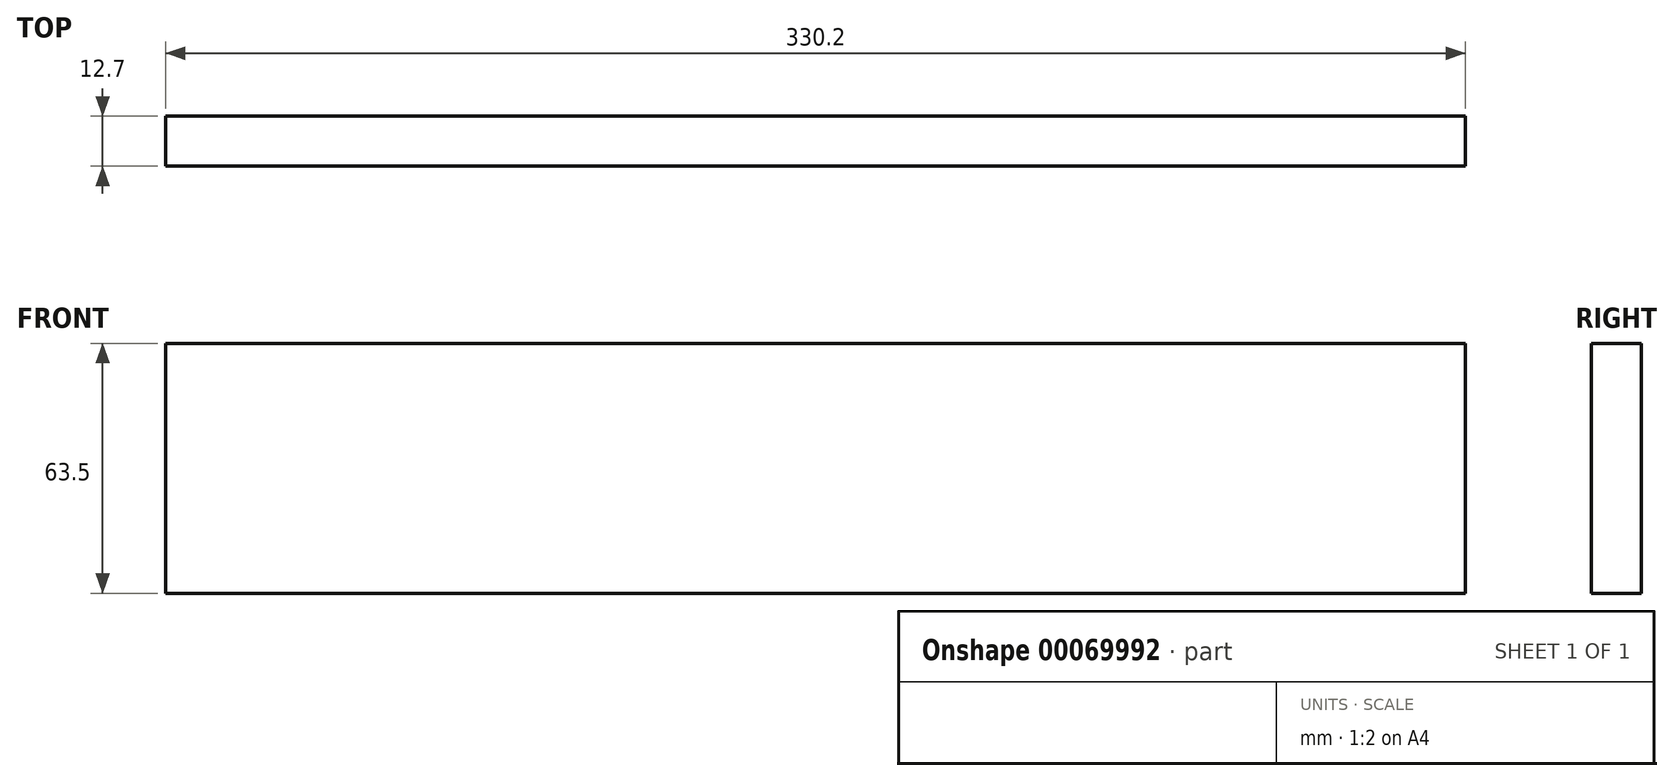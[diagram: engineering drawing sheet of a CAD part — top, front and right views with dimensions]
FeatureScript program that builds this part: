
annotation { "Feature Type Name" : "Feature", "Feature Type Description" : "" }
export const myFeature = defineFeature(function(context is Context, id is Id, definition is map)
    precondition{}
    {
        {
            var Q0;
            Q0=qCreatedBy(makeId("Front.planeOp"),FACE);
            var sketch = newSketch(context, id + "F0", { "sketchPlane" : qUnion([Q0])});
            skLineSegment(sketch, "E0.rect.bottom", {"start": v(165.1, 31.75) * mm, "end": v(-165.1, 31.75) * mm});
            skLineSegment(sketch, "E0.rect.top", {"start": v(165.1, -31.75) * mm, "end": v(-165.1, -31.75) * mm});
            skLineSegment(sketch, "E0.rect.left", {"start": v(165.1, 31.75) * mm, "end": v(165.1, -31.75) * mm});
            skLineSegment(sketch, "E0.rect.right", {"start": v(-165.1, 31.75) * mm, "end": v(-165.1, -31.75) * mm});
            skPoint(sketch, "E0.rect.middle", {"position": v(0, 0) * mm});
            skSolve(sketch);
        }
        {
            var Q0;
            Q0=makeQuery(id+"F0.imprint","IMPRINT",FACE,{"disambiguationData":[TD([[makeQuery(id+"F0.imprint","IMPRINT",EDGE,{"derivedFrom":sQuery(id+"F0.wireOp",EDGE,"E0.rect.bottom")}),1.0]])]});
            extrude(context, id + "F1", {"entities" : qUnion([Q0]), "depth" : 12.7 * mm});
        }
    });
